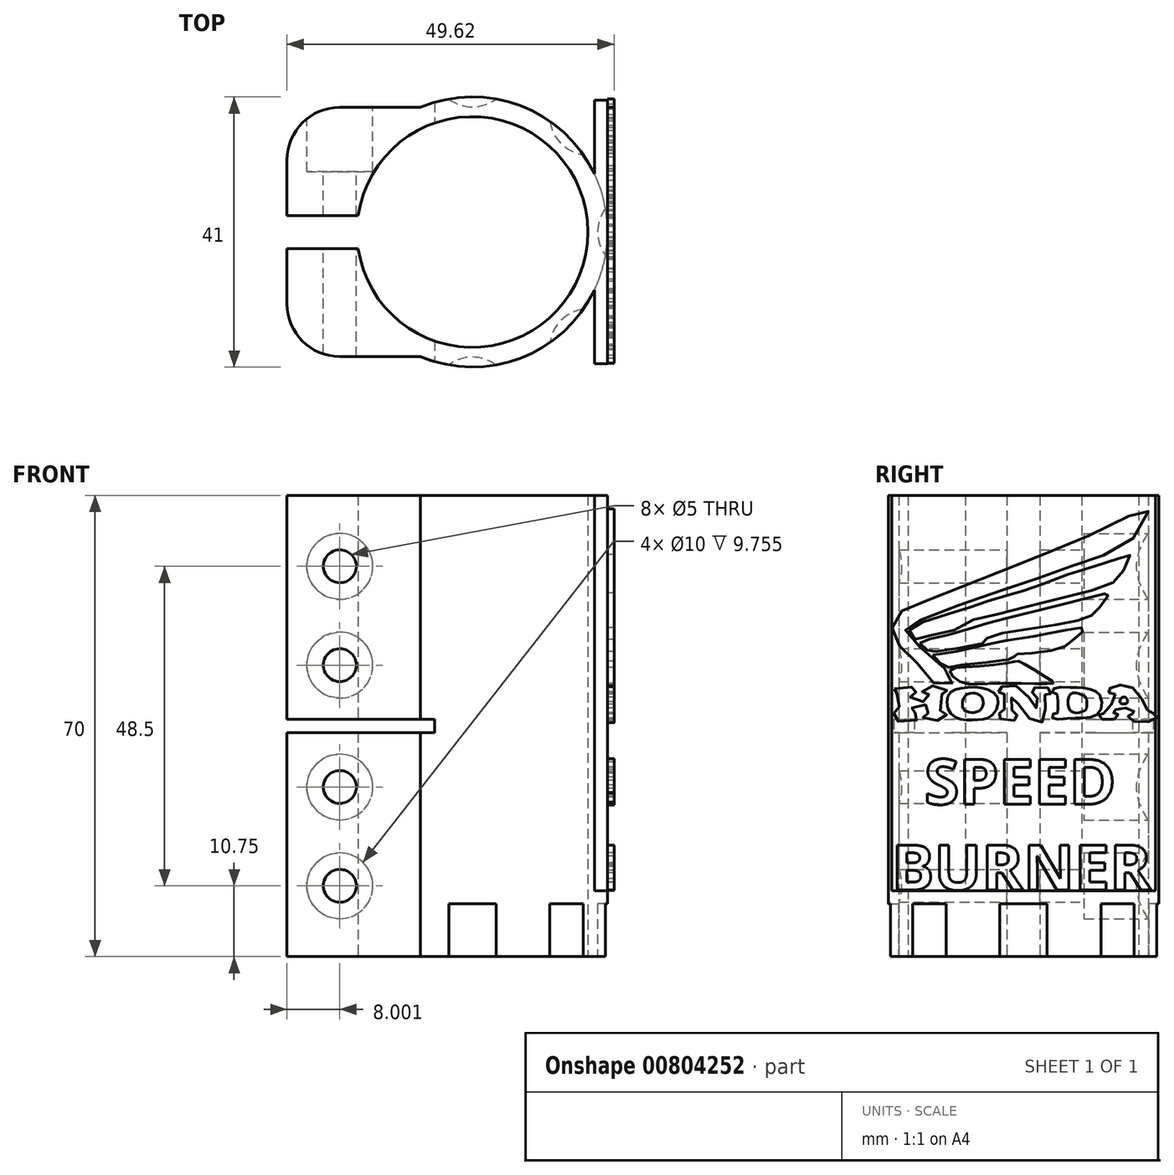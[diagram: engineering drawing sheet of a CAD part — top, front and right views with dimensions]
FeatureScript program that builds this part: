
annotation { "Feature Type Name" : "Feature", "Feature Type Description" : "" }
export const myFeature = defineFeature(function(context is Context, id is Id, definition is map)
    precondition{}
    {
        {
            var Q0;
            Q0=qCreatedBy(makeId("Top.planeOp"),FACE);
            var sketch = newSketch(context, id + "F0", { "sketchPlane" : qUnion([Q0])});
            skArc(sketch, "E0", {"start": v(-17.32, -2.5) * mm, "mid": v(17.5, 0) * mm, "end": v(-17.32, 2.5) * mm});
            skArc(sketch, "E1", {"start": v(-7.92, -18.9) * mm, "mid": v(20.5, 0) * mm, "end": v(-7.92, 18.9) * mm});
            skLineSegment(sketch, "E2", {"start": v(-17.32, 2.5) * mm, "end": v(-28.12, 2.5) * mm});
            skLineSegment(sketch, "E3", {"start": v(-28.12, 2.5) * mm, "end": v(-28.12, 10.9) * mm});
            skLineSegment(sketch, "E4", {"start": v(-20.12, 18.9) * mm, "end": v(-7.92, 18.9) * mm});
            skPoint(sketch, "E5.visualSharp", {"position": v(-28.12, 18.9) * mm});
            skArc(sketch, "E5.filletArc", {"start": v(-20.12, 18.9) * mm, "mid": v(-25.78, 16.57) * mm, "end": v(-28.12, 10.9) * mm});
            skLineSegment(sketch, "E6", {"start": v(0, 0) * mm, "end": v(34.28, 0) * mm, "construction": true});
            skArc(sketch, "E7.MirrorCS", {"start": v(-20.12, -18.9) * mm, "mid": v(-25.78, -16.57) * mm, "end": v(-28.12, -10.9) * mm});
            skLineSegment(sketch, "E8.MirrorCS", {"start": v(-20.12, -18.9) * mm, "end": v(-7.92, -18.9) * mm});
            skLineSegment(sketch, "E9.MirrorCS", {"start": v(-28.12, -2.5) * mm, "end": v(-28.12, -10.9) * mm});
            skLineSegment(sketch, "E10.MirrorCS", {"start": v(-17.32, -2.5) * mm, "end": v(-28.12, -2.5) * mm});
            skSolve(sketch);
        }
        {
            var Q0;
            Q0=makeQuery(id+"F0.imprint","IMPRINT",FACE,{"disambiguationData":[TD([[makeQuery(id+"F0.imprint","IMPRINT",EDGE,{"derivedFrom":sQuery(id+"F0.wireOp",EDGE,"E0")}),-1.0]])]});
            extrude(context, id + "F1", {"entities" : qUnion([Q0]), "endBound" : BoundingType.SYMMETRIC, "depth" : 70 * mm, "offsetDistance" : 25 * mm});
        }
        {
            var Q0;
            Q0=makeQuery(id+"F1.opExtrude","SWEPT_FACE",FACE,{"disambiguationData":[OSD([sQuery(id+"F0.wireOp",EDGE,"E4")])]});
            var sketch = newSketch(context, id + "F2", { "sketchPlane" : qUnion([Q0])});
            skPoint(sketch, "E11", {"position": v(20.12, -24.25) * mm});
            skPoint(sketch, "E12", {"position": v(20.12, -9.25) * mm});
            skPoint(sketch, "E13", {"position": v(20.12, 9.25) * mm});
            skPoint(sketch, "E14", {"position": v(20.12, 24.25) * mm});
            skSolve(sketch);
        }
        {
            var Q0;
            Q0=sQuery(id+"F2.wireOp",VERTEX,"E11");
            var Q1;
            Q1=sQuery(id+"F2.wireOp",VERTEX,"E12");
            var Q2;
            Q2=sQuery(id+"F2.wireOp",VERTEX,"E13");
            var Q3;
            Q3=sQuery(id+"F2.wireOp",VERTEX,"E14");
            var Q4;
            Q4=makeQuery(id+"F1.opExtrude","SWEPT_BODY",BODY,{"disambiguationData":[OSD([sQuery(id+"F0.wireOp",EDGE,"E0"),sQuery(id+"F0.wireOp",EDGE,"E1"),sQuery(id+"F0.wireOp",EDGE,"E2"),sQuery(id+"F0.wireOp",EDGE,"E3"),sQuery(id+"F0.wireOp",EDGE,"E4"),sQuery(id+"F0.wireOp",EDGE,"E5.filletArc"),sQuery(id+"F0.wireOp",EDGE,"E7.MirrorCS"),sQuery(id+"F0.wireOp",EDGE,"E8.MirrorCS"),sQuery(id+"F0.wireOp",EDGE,"E9.MirrorCS"),sQuery(id+"F0.wireOp",EDGE,"E10.MirrorCS")])]});
            hole(context, id + "F3", {"style" : HoleStyle.C_BORE, "endStyle" : HoleEndStyle.THROUGH, "holeDiameter" : 5 * mm, "cBoreDiameter" : 10 * mm, "cBoreDepth" : 8 * mm, "majorDiameter" : 5 * mm, "isTappedThrough" : true, "tappedDepth" : 12 * mm, "tapClearance" : 3, "locations" : qUnion([Q0, Q1, Q2, Q3]), "scope" : qUnion([Q4])});
        }
        {
            var Q0;
            Q0=qCreatedBy(makeId("Front.planeOp"),FACE);
            var sketch = newSketch(context, id + "F4", { "sketchPlane" : qUnion([Q0])});
            skLineSegment(sketch, "E15.bottom", {"start": v(-28.12, -1) * mm, "end": v(-5.72, -1) * mm});
            skLineSegment(sketch, "E15.top", {"start": v(-28.12, 1) * mm, "end": v(-5.72, 1) * mm});
            skLineSegment(sketch, "E15.left", {"start": v(-28.12, -1) * mm, "end": v(-28.12, 1) * mm});
            skLineSegment(sketch, "E15.right", {"start": v(-5.72, -1) * mm, "end": v(-5.72, 1) * mm});
            skSolve(sketch);
        }
        {
            var Q0;
            Q0 = qSketchRegion(id + "F4", true);
            extrude(context, id + "F5", {"entities" : qUnion([Q0]), "operationType" : NewBodyOperationType.REMOVE, "endBound" : BoundingType.SYMMETRIC, "oppositeDirection" : true, "depth" : 50 * mm, "offsetDistance" : 25 * mm});
        }
        {
            var Q0;
            Q0=makeQuery(id+"F1.opExtrude","CAP_FACE",FACE,{"disambiguationData":[OSD([sQuery(id+"F0.wireOp",EDGE,"E0"),sQuery(id+"F0.wireOp",EDGE,"E1"),sQuery(id+"F0.wireOp",EDGE,"E2"),sQuery(id+"F0.wireOp",EDGE,"E3"),sQuery(id+"F0.wireOp",EDGE,"E4"),sQuery(id+"F0.wireOp",EDGE,"E5.filletArc"),sQuery(id+"F0.wireOp",EDGE,"E7.MirrorCS"),sQuery(id+"F0.wireOp",EDGE,"E8.MirrorCS"),sQuery(id+"F0.wireOp",EDGE,"E9.MirrorCS"),sQuery(id+"F0.wireOp",EDGE,"E10.MirrorCS")])],"isStart":true});
            var sketch = newSketch(context, id + "F6", { "sketchPlane" : qUnion([Q0])});
            skCircle(sketch, "E16", {"center": v(0, -25) * mm, "radius": 6 * mm});
            skCircle(sketch, "E17.1.0", {"center": v(17.68, -17.68) * mm, "radius": 6 * mm});
            skCircle(sketch, "E17.2.0", {"center": v(25, 0) * mm, "radius": 6 * mm});
            skCircle(sketch, "E17.3.0", {"center": v(17.68, 17.68) * mm, "radius": 6 * mm});
            skCircle(sketch, "E17.4.0", {"center": v(0, 25) * mm, "radius": 6 * mm});
            skPoint(sketch, "E17.center", {"position": v(0, 0) * mm});
            skLineSegment(sketch, "E17.anchor1", {"start": v(0, 0) * mm, "end": v(0, -25) * mm, "construction": true});
            skLineSegment(sketch, "E17.anchor2", {"start": v(0, 0) * mm, "end": v(0, 25) * mm, "construction": true});
            skSolve(sketch);
        }
        {
            var Q0;
            {var subQ0=sQuery(id+"F6.wireOp",EDGE,"E17.4.0");var subQ1=makeQuery(id+"F1.opExtrude","CAP_EDGE",EDGE,{"disambiguationData":[OSD([sQuery(id+"F0.wireOp",EDGE,"E1")])],"isStart":true});var subQ2=makeQuery(id+"F6.imprint","INTERSECT",VERTEX,{"disambiguationData":[OD(0.0)],"derivedFrom":[subQ1,subQ0]});Q0=makeQuery(id+"F6.imprint","IMPRINT",FACE,{"disambiguationData":[TD([[makeQuery(id+"F6.imprint","IMPRINT",EDGE,{"disambiguationData":[TD([[subQ2,1.0]])],"derivedFrom":subQ0}),1.0]])]});}
            var Q1;
            {var subQ0=sQuery(id+"F6.wireOp",EDGE,"E17.3.0");var subQ1=makeQuery(id+"F1.opExtrude","CAP_EDGE",EDGE,{"disambiguationData":[OSD([sQuery(id+"F0.wireOp",EDGE,"E1")])],"isStart":true});var subQ2=makeQuery(id+"F6.imprint","INTERSECT",VERTEX,{"disambiguationData":[OD(0.0)],"derivedFrom":[subQ1,subQ0]});Q1=makeQuery(id+"F6.imprint","IMPRINT",FACE,{"disambiguationData":[TD([[makeQuery(id+"F6.imprint","IMPRINT",EDGE,{"disambiguationData":[TD([[subQ2,1.0]])],"derivedFrom":subQ0}),1.0]])]});}
            var Q2;
            {var subQ0=sQuery(id+"F6.wireOp",EDGE,"E17.2.0");var subQ1=makeQuery(id+"F1.opExtrude","CAP_EDGE",EDGE,{"disambiguationData":[OSD([sQuery(id+"F0.wireOp",EDGE,"E1")])],"isStart":true});var subQ2=makeQuery(id+"F6.imprint","INTERSECT",VERTEX,{"disambiguationData":[OD(0.0)],"derivedFrom":[subQ1,subQ0]});Q2=makeQuery(id+"F6.imprint","IMPRINT",FACE,{"disambiguationData":[TD([[makeQuery(id+"F6.imprint","IMPRINT",EDGE,{"disambiguationData":[TD([[subQ2,-1.0]])],"derivedFrom":subQ0}),1.0]])]});}
            var Q3;
            {var subQ0=sQuery(id+"F6.wireOp",EDGE,"E17.1.0");var subQ1=makeQuery(id+"F1.opExtrude","CAP_EDGE",EDGE,{"disambiguationData":[OSD([sQuery(id+"F0.wireOp",EDGE,"E1")])],"isStart":true});var subQ2=makeQuery(id+"F6.imprint","INTERSECT",VERTEX,{"disambiguationData":[OD(0.0)],"derivedFrom":[subQ1,subQ0]});Q3=makeQuery(id+"F6.imprint","IMPRINT",FACE,{"disambiguationData":[TD([[makeQuery(id+"F6.imprint","IMPRINT",EDGE,{"disambiguationData":[TD([[subQ2,-1.0]])],"derivedFrom":subQ0}),1.0]])]});}
            var Q4;
            {var subQ0=sQuery(id+"F6.wireOp",EDGE,"E16");var subQ1=makeQuery(id+"F1.opExtrude","CAP_EDGE",EDGE,{"disambiguationData":[OSD([sQuery(id+"F0.wireOp",EDGE,"E1")])],"isStart":true});var subQ2=makeQuery(id+"F6.imprint","INTERSECT",VERTEX,{"disambiguationData":[OD(0.0)],"derivedFrom":[subQ1,subQ0]});Q4=makeQuery(id+"F6.imprint","IMPRINT",FACE,{"disambiguationData":[TD([[makeQuery(id+"F6.imprint","IMPRINT",EDGE,{"disambiguationData":[TD([[subQ2,-1.0]])],"derivedFrom":subQ0}),1.0]])]});}
            var Q5;
            {var subQ0=sQuery(id+"F6.wireOp",EDGE,"E16");var subQ1=makeQuery(id+"F1.opExtrude","CAP_EDGE",EDGE,{"disambiguationData":[OSD([sQuery(id+"F0.wireOp",EDGE,"E1")])],"isStart":true});var subQ2=makeQuery(id+"F6.imprint","INTERSECT",VERTEX,{"disambiguationData":[OD(0.0)],"derivedFrom":[subQ1,subQ0]});Q5=makeQuery(id+"F6.imprint","IMPRINT",FACE,{"disambiguationData":[TD([[makeQuery(id+"F6.imprint","IMPRINT",EDGE,{"disambiguationData":[TD([[subQ2,1.0]])],"derivedFrom":subQ0}),1.0]])]});}
            var Q6;
            {var subQ0=sQuery(id+"F6.wireOp",EDGE,"E17.1.0");var subQ1=makeQuery(id+"F1.opExtrude","CAP_EDGE",EDGE,{"disambiguationData":[OSD([sQuery(id+"F0.wireOp",EDGE,"E1")])],"isStart":true});var subQ2=makeQuery(id+"F6.imprint","INTERSECT",VERTEX,{"disambiguationData":[OD(0.0)],"derivedFrom":[subQ1,subQ0]});Q6=makeQuery(id+"F6.imprint","IMPRINT",FACE,{"disambiguationData":[TD([[makeQuery(id+"F6.imprint","IMPRINT",EDGE,{"disambiguationData":[TD([[subQ2,1.0]])],"derivedFrom":subQ0}),1.0]])]});}
            var Q7;
            {var subQ0=sQuery(id+"F6.wireOp",EDGE,"E17.2.0");var subQ1=makeQuery(id+"F1.opExtrude","CAP_EDGE",EDGE,{"disambiguationData":[OSD([sQuery(id+"F0.wireOp",EDGE,"E1")])],"isStart":true});var subQ2=makeQuery(id+"F6.imprint","INTERSECT",VERTEX,{"disambiguationData":[OD(0.0)],"derivedFrom":[subQ1,subQ0]});Q7=makeQuery(id+"F6.imprint","IMPRINT",FACE,{"disambiguationData":[TD([[makeQuery(id+"F6.imprint","IMPRINT",EDGE,{"disambiguationData":[TD([[subQ2,1.0]])],"derivedFrom":subQ0}),1.0]])]});}
            var Q8;
            {var subQ0=sQuery(id+"F6.wireOp",EDGE,"E17.3.0");var subQ1=makeQuery(id+"F1.opExtrude","CAP_EDGE",EDGE,{"disambiguationData":[OSD([sQuery(id+"F0.wireOp",EDGE,"E1")])],"isStart":true});var subQ2=makeQuery(id+"F6.imprint","INTERSECT",VERTEX,{"disambiguationData":[OD(0.0)],"derivedFrom":[subQ1,subQ0]});Q8=makeQuery(id+"F6.imprint","IMPRINT",FACE,{"disambiguationData":[TD([[makeQuery(id+"F6.imprint","IMPRINT",EDGE,{"disambiguationData":[TD([[subQ2,-1.0]])],"derivedFrom":subQ0}),1.0]])]});}
            var Q9;
            {var subQ0=sQuery(id+"F6.wireOp",EDGE,"E17.4.0");var subQ1=makeQuery(id+"F1.opExtrude","CAP_EDGE",EDGE,{"disambiguationData":[OSD([sQuery(id+"F0.wireOp",EDGE,"E1")])],"isStart":true});var subQ2=makeQuery(id+"F6.imprint","INTERSECT",VERTEX,{"disambiguationData":[OD(0.0)],"derivedFrom":[subQ1,subQ0]});Q9=makeQuery(id+"F6.imprint","IMPRINT",FACE,{"disambiguationData":[TD([[makeQuery(id+"F6.imprint","IMPRINT",EDGE,{"disambiguationData":[TD([[subQ2,-1.0]])],"derivedFrom":subQ0}),1.0]])]});}
            extrude(context, id + "F7", {"entities" : qUnion([Q0, Q1, Q2, Q3, Q4, Q5, Q6, Q7, Q8, Q9]), "operationType" : NewBodyOperationType.REMOVE, "oppositeDirection" : true, "depth" : 8 * mm, "offsetDistance" : 25 * mm});
        }
        {
            var Q0;
            Q0=qCreatedBy(makeId("Right.planeOp"),FACE);
            cPlane(context, id + "F8", {"entities" : qUnion([Q0]), "cplaneType" : CPlaneType.OFFSET, "offset" : 20.5 * mm, "width" : 150 * mm, "height" : 150 * mm});
        }
        {
            var Q0;
            Q0=qCreatedBy(id+"F8.planeOp",FACE);
            var sketch = newSketch(context, id + "F9", { "sketchPlane" : qUnion([Q0])});
            skLineSegment(sketch, "E18.bottom", {"start": v(-20, 35) * mm, "end": v(20, 35) * mm});
            skLineSegment(sketch, "E18.top", {"start": v(-20, -25) * mm, "end": v(20, -25) * mm});
            skLineSegment(sketch, "E18.left", {"start": v(-20, 35) * mm, "end": v(-20, -25) * mm});
            skLineSegment(sketch, "E18.right", {"start": v(20, 35) * mm, "end": v(20, -25) * mm});
            skSolve(sketch);
        }
        {
            var Q0;
            Q0 = qSketchRegion(id + "F9", true);
            extrude(context, id + "F10", {"entities" : qUnion([Q0]), "operationType" : NewBodyOperationType.ADD, "oppositeDirection" : true, "depth" : 2 * mm, "offsetDistance" : 25 * mm});
        }
        {
            var Q0;
            Q0=makeQuery(id+"F10.opExtrude","CAP_FACE",FACE,{"disambiguationData":[OSD([sQuery(id+"F9.wireOp",EDGE,"E18.bottom"),sQuery(id+"F9.wireOp",EDGE,"E18.top"),sQuery(id+"F9.wireOp",EDGE,"E18.left"),sQuery(id+"F9.wireOp",EDGE,"E18.right")])],"isStart":true});
            var sketch = newSketch(context, id + "F11", { "sketchPlane" : qUnion([Q0])});
            skText(sketch, "E19", { "text": "  SPEED \nBURNER", "fontName": "OpenSans-Bold.ttf"});
            skFitSpline(sketch, "E20", {"points": [v(-13.64, 6.56) * mm, v(-16.33, 9.8) * mm, v(-18.84, 12.17) * mm, v(-19.91, 14.38) * mm, v(-19.41, 16.67) * mm, v(-16.1, 18.51) * mm, v(-8.96, 21.28) * mm, v(1.77, 25.55) * mm, v(14.78, 31.2) * mm, v(18.86, 32.87) * mm, v(16.65, 28.5) * mm, v(10.2, 25.31) * mm, v(3.52, 22.88) * mm, v(-5.44, 19.89) * mm, v(-16.12, 15.88) * mm, v(-17.89, 14.79) * mm, v(-17.33, 13.6) * mm, v(-13.22, 9.84) * mm, v(-10.6, 6.95) * mm, v(-11.3, 6.26) * mm, v(-13.64, 6.56) * mm]});
            skPoint(sketch, "E21.1.internal.orphan", {"position": v(-15.53, 13.6) * mm});
            skPoint(sketch, "E21.13.internal.orphan", {"position": v(-16.95, 14.79) * mm});
            skPoint(sketch, "E22", {"position": v(-16.9, 13.51) * mm});
            skFitSpline(sketch, "E23", {"points": [v(-16.47, 13.18) * mm, v(-12.78, 14.13) * mm, v(-9.14, 14.97) * mm, v(-9.12, 15.53) * mm, v(-6.42, 16.4) * mm, v(2.96, 18.73) * mm, v(12.94, 21.48) * mm, v(14.93, 23.27) * mm, v(16.13, 25.96) * mm, v(14.73, 25.56) * mm, v(7.76, 23.37) * mm, v(1.1, 20.89) * mm, v(-2.06, 19.94) * mm, v(-6.27, 18.68) * mm, v(-9.8, 17.45) * mm, v(-16.67, 15.22) * mm, v(-17.3, 14.26) * mm, v(-16.47, 13.18) * mm]});
            skFitSpline(sketch, "E24", {"points": [v(-15.74, 12.58) * mm, v(-14.45, 11.45) * mm, v(-13.36, 11.33) * mm, v(-5.67, 12.83) * mm, v(-5.54, 13.28) * mm, v(2.23, 14.97) * mm, v(9.7, 16.47) * mm, v(11.51, 17.98) * mm, v(12.93, 20.1) * mm, v(12.31, 20.12) * mm, v(4.37, 18.1) * mm, v(-1.2, 16.7) * mm, v(-6.4, 15.35) * mm, v(-13.09, 13.45) * mm, v(-15.74, 12.58) * mm]});
            skFitSpline(sketch, "E25", {"points": [v(-13.79, 10.78) * mm, v(-11.87, 9.04) * mm, v(-10.64, 9.07) * mm, v(-1.77, 10.18) * mm, v(-1.35, 10.48) * mm, v(-1.38, 10.78) * mm, v(0, 10.96) * mm, v(5.9, 11.9) * mm, v(7.42, 13.03) * mm, v(9.25, 14.79) * mm, v(5.66, 14.44) * mm, v(0.86, 13.5) * mm, v(-2.82, 12.94) * mm, v(-7.73, 11.86) * mm, v(-13.22, 10.9) * mm, v(-13.79, 10.78) * mm]});
            skFitSpline(sketch, "E26", {"points": [v(-11.16, 8.4) * mm, v(-9.35, 6.63) * mm, v(-5.59, 6.44) * mm, v(0.4, 6.44) * mm, v(4.6, 6.54) * mm, v(4, 7.03) * mm, v(-0.51, 9.77) * mm, v(-1.13, 9.84) * mm, v(-6.9, 9.07) * mm, v(-11.16, 8.4) * mm]});
            skFitSpline(sketch, "E27", {"points": [v(-19.63, 5.67) * mm, v(-16.27, 5.67) * mm, v(-16.2, 5.2) * mm, v(-16.98, 4.92) * mm, v(-17.01, 4.1) * mm, v(-14.5, 3.95) * mm, v(-14.43, 4.86) * mm, v(-15.24, 4.98) * mm, v(-15.11, 5.79) * mm, v(-11.88, 5.73) * mm, v(-11.66, 5.14) * mm, v(-12.31, 4.92) * mm, v(-12.5, 2) * mm, v(-11.78, 1.85) * mm, v(-11.67, 1.33) * mm, v(-15.07, 1) * mm, v(-15.1, 1.71) * mm, v(-14.5, 1.96) * mm, v(-14.4, 2.98) * mm, v(-16.79, 2.94) * mm, v(-16.93, 2.06) * mm, v(-16.22, 1.92) * mm, v(-16.08, 1) * mm, v(-19.59, 1) * mm, v(-19.7, 1.89) * mm, v(-19.17, 2.03) * mm, v(-18.96, 4.83) * mm, v(-19.73, 5.11) * mm, v(-19.63, 5.67) * mm]});
            skFitSpline(sketch, "E28", {"points": [v(-9.29, 3.3) * mm, v(-8.51, 4.83) * mm, v(-6.41, 4.48) * mm, v(-6.34, 2.73) * mm, v(-7.6, 2.03) * mm, v(-8.9, 2.38) * mm, v(-9.29, 3.3) * mm]});
            skFitSpline(sketch, "E29", {"points": [v(-9.5, 5.74) * mm, v(-5.96, 5.7) * mm, v(-3.85, 4) * mm, v(-4.94, 1.5) * mm, v(-6.87, 1) * mm, v(-9.32, 1) * mm, v(-11.3, 2.3) * mm, v(-11.3, 4.83) * mm, v(-9.5, 5.74) * mm]});
            skFitSpline(sketch, "E30", {"points": [v(-3.78, 5.15) * mm, v(-3.08, 5.15) * mm, v(-3.12, 2.03) * mm, v(-3.68, 1.92) * mm, v(-3.78, 1.33) * mm, v(-1.05, 1) * mm, v(-0.98, 1.64) * mm, v(-1.57, 2) * mm, v(-1.75, 4.38) * mm, v(0.74, 1.3) * mm, v(3.2, 1) * mm, v(3.3, 4.83) * mm, v(4, 4.83) * mm, v(4.14, 5.6) * mm, v(1.44, 5.7) * mm, v(1.23, 5.15) * mm, v(1.9, 4.83) * mm, v(2, 2.76) * mm, v(-0.45, 5.78) * mm, v(-3.68, 5.7) * mm, v(-3.78, 5.15) * mm]});
            skFitSpline(sketch, "E31", {"points": [v(4.52, 5.66) * mm, v(4.45, 5.15) * mm, v(5.05, 4.83) * mm, v(5.21, 2.81) * mm, v(5.16, 1.96) * mm, v(4.52, 1.86) * mm, v(4.43, 1.16) * mm, v(6.7, 1.18) * mm, v(8.98, 1.23) * mm, v(10.9, 1.6) * mm, v(11.87, 3.03) * mm, v(11.47, 4.83) * mm, v(10.36, 5.54) * mm, v(8.82, 5.82) * mm, v(7.16, 5.85) * mm, v(4.52, 5.66) * mm]});
            skFitSpline(sketch, "E32", {"points": [v(7.13, 4.83) * mm, v(7.14, 2.3) * mm, v(9.01, 2.2) * mm, v(9.51, 2.65) * mm, v(9.53, 4.16) * mm, v(9.03, 4.66) * mm, v(7.13, 4.83) * mm]});
            skFitSpline(sketch, "E33", {"points": [v(13.9, 4.83) * mm, v(12.95, 5.08) * mm, v(13.03, 5.71) * mm, v(16.6, 5.8) * mm, v(19.07, 2.15) * mm, v(20, 1.81) * mm, v(20, 1) * mm, v(16.04, 1) * mm, v(16.01, 1.76) * mm, v(16.78, 1.89) * mm, v(16.51, 2.44) * mm, v(13.98, 2.52) * mm, v(13.59, 2.05) * mm, v(14.2, 1.92) * mm, v(14.27, 1.3) * mm, v(11.53, 1.23) * mm, v(11.5, 1.73) * mm, v(12.1, 1.89) * mm, v(13.9, 4.83) * mm]});
            skFitSpline(sketch, "E34", {"points": [v(14.7, 3.51) * mm, v(15.16, 4.42) * mm, v(15.78, 3.62) * mm, v(14.7, 3.51) * mm]});
            const initialGuessF11  = {"E19": [-0.02, -0.01188, 1, 0, 0.00688]};
            skSetInitialGuess(sketch, initialGuessF11);
            skSolve(sketch);
        }
        {
            var Q0;
            Q0 = qSketchRegion(id + "F11", true);
            extrude(context, id + "F12", {"entities" : qUnion([Q0]), "operationType" : NewBodyOperationType.ADD, "depth" : 1 * mm, "offsetDistance" : 25 * mm});
        }
    });
